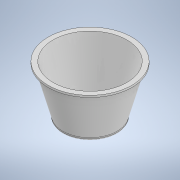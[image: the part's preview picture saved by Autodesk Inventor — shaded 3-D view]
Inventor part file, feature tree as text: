
AUTODESK INVENTOR PART (.ipt)
format: ipt  version: 2020 (Build 240168000, 168)  size: 140,288 bytes
history: native  units: mm
features: sketch x2, revolve x1, fillet x1
ambient origin geometry x8: Origin, YZ Plane, XZ Plane, XY Plane, X Axis, Y Axis, Z Axis, Center Point
bodies: Solid1 (feature_tree)
feature tree (4):
  sketch  "Sketch1"  dims[d0=25.0mm d1=50.0mm d2=105.0deg]
  sketch  "Sketch2"  dims[d3=5.0mm d4=2.0mm d5=3.0mm d6=105.0deg d7=3.0mm d8=90.0deg d9=2.0mm d10=0.5mm d11=0.872665mm]
  revolve  "Revolution1"  [1 undecoded]
  fillet  "Fillet1"  [1 undecoded]
note: 2 required parameter values undecoded (feature->parameter linkage not recoverable at this tier; creation-order binding heuristic only, values carry confidence <= 0.55)